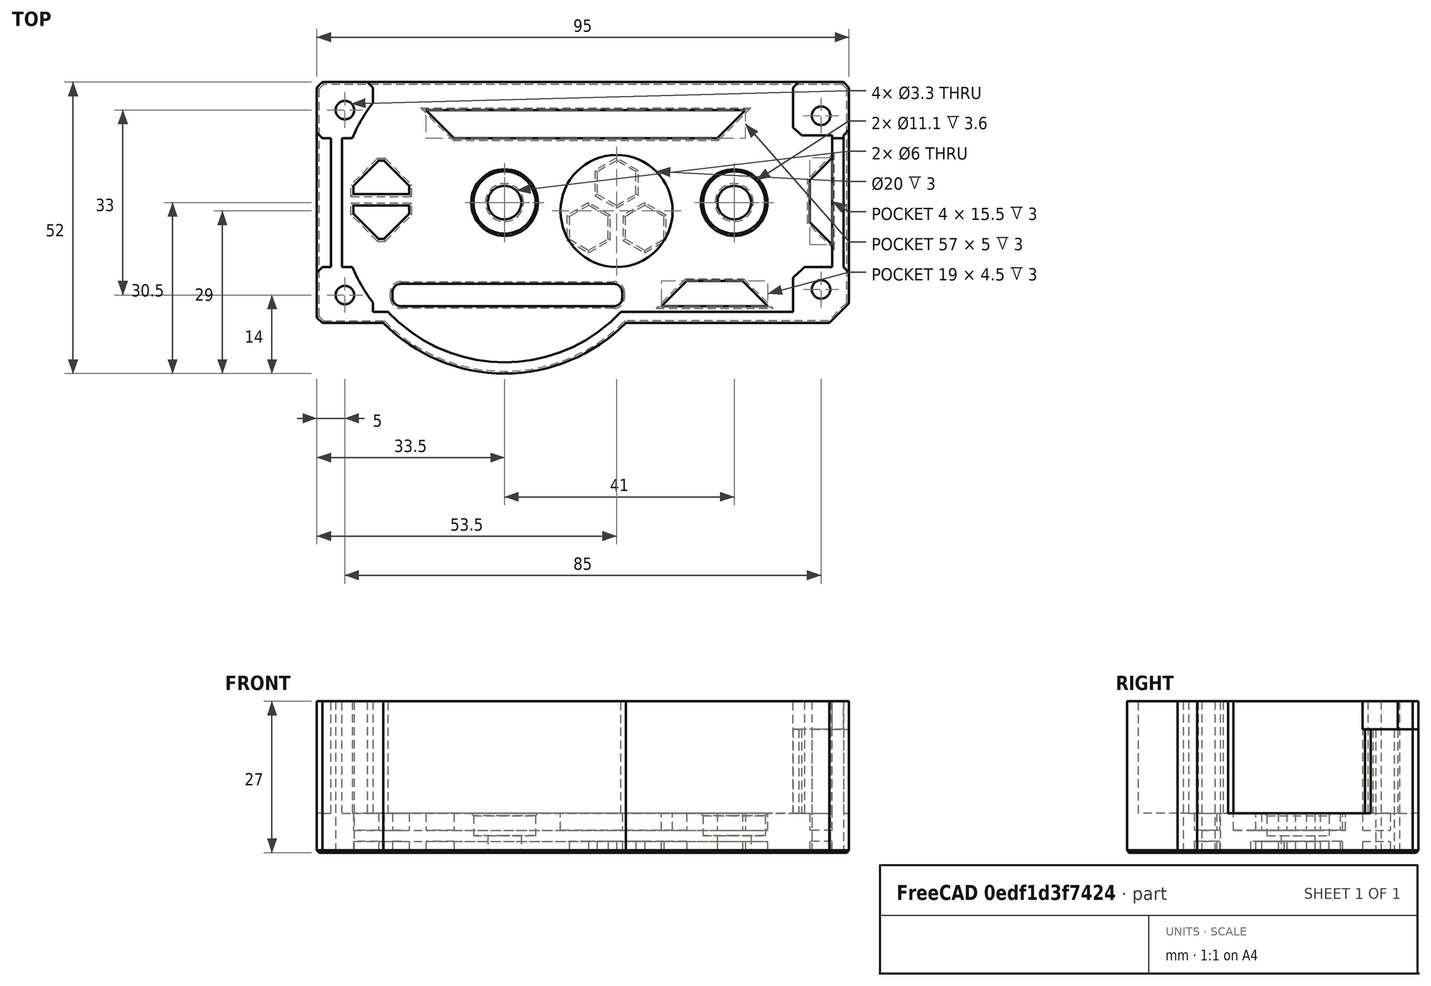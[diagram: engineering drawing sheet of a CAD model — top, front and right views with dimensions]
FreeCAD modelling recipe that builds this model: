
FCSTD DOCUMENT  (FreeCAD 0.19R24291 (Git))
Label: front-plate-type-1
License: Other
LicenseURL: GPL3
objects: Part::Box×14, Part::MultiFuse×6, Part::Chamfer×4, Part::Cylinder×3, Part::Feature×2, Part::Cut×2, Part::Refine×2, Part::MultiCommon×1
note: 34 computed .brp shape members not serialized (recipe doc carries the construction recipe); baked Part::Feature solids carry a one-line shape summary decoded from their .brp

FEATURE [Part::Feature] Chamfer029006001  label="front-plate-type001"
  Placement = pos=(27.5,-8.5,7) rot=(0,1,0;3.14159rad)
  shape: bbox 95 x 43 x 27 mm, 156 faces (baked)
FEATURE [Part::Box] Box  label="Cube"
  AttacherType = Attacher::AttachEngine3D
  Height = 26.5
  Length = 2
  Placement = pos=(-44.5,-12,0.5) rot=(0,0,1;0rad)
  Width = 24
FEATURE [Part::Box] Box001  label="Cube001"
  AttacherType = Attacher::AttachEngine3D
  Height = 7
  Length = 69
  Placement = pos=(-33,16.5,0) rot=(0,0,1;0rad)
  Width = 5
FEATURE [Part::Chamfer] Chamfer
  Base = -> Box001
  Edges = 2 edges r=0.4: [Edge9,Edge11]
FEATURE [Part::Box] Box002  label="Cube002"
  AttacherType = Attacher::AttachEngine3D
  Height = 7
  Length = 28
  Placement = pos=(11,-21.5,0) rot=(0,0,1;0rad)
  Width = 3
FEATURE [Part::Chamfer] Chamfer029006002
  Base = -> Box002
  Edges = 2 edges r=0.4: [Edge9,Edge11]
FEATURE [Part::Box] Box003  label="Cube003"
  AttacherType = Attacher::AttachEngine3D
  Height = 7
  Length = 3
  Placement = pos=(45,-11,0) rot=(0,0,1;0rad)
  Width = 23
FEATURE [Part::Chamfer] Chamfer029006003
  Base = -> Box003
  Edges = 2 edges r=0.4: [Edge4,Edge8]
FEATURE [Part::MultiFuse] Fusion
  Shapes = -> [Chamfer029006001,Chamfer029006002,Chamfer029006003,Chamfer]
FEATURE [Part::Box] Box004  label="Cube004"
  AttacherType = Attacher::AttachEngine3D
  Height = 26.5
  Length = 2
  Placement = pos=(45,-12,0.5) rot=(0,0,1;0rad)
  Width = 23.5
FEATURE [Part::Box] Box005  label="Cube005"
  AttacherType = Attacher::AttachEngine3D
  Height = 21.5
  Length = 2
  Placement = pos=(45,11.5,0.5) rot=(0,0,1;0rad)
  Width = 1.5
FEATURE [Part::Box] Box006  label="Cube006"
  AttacherType = Attacher::AttachEngine3D
  Height = 26.5
  Length = 29
  Placement = pos=(11.5,-21.5,0.5) rot=(0,0,1;0rad)
  Width = 2
FEATURE [Part::Box] Box007  label="Cube007"
  AttacherType = Attacher::AttachEngine3D
  Height = 2
  Length = 12
  Placement = pos=(-41.5,-7,5) rot=(0,0,1;0rad)
  Width = 15
FEATURE [Part::Box] Box008  label="Cube008"
  AttacherType = Attacher::AttachEngine3D
  Height = 2
  Length = 19
  Placement = pos=(-3,-9,5) rot=(0,0,1;0rad)
  Width = 17
FEATURE [Part::Box] Box009  label="Cube009"
  AttacherType = Attacher::AttachEngine3D
  Height = 2
  Length = 69
  Placement = pos=(-34,-19.5,5) rot=(0,0,1;0rad)
  Width = 6
FEATURE [Part::Box] Box010  label="Cube010"
  AttacherType = Attacher::AttachEngine3D
  Height = 2
  Length = 59
  Placement = pos=(-28.5,10.5,5) rot=(0,0,1;0rad)
  Width = 7
FEATURE [Part::Box] Box011  label="Cube011"
  AttacherType = Attacher::AttachEngine3D
  Height = 2
  Length = 6
  Placement = pos=(40.5,-8,5) rot=(0,0,1;0rad)
  Width = 17
FEATURE [Part::MultiFuse] Fusion002
  Placement = pos=(0,0,-3) rot=(0,0,1;0rad)
  Shapes = -> [Box011,Box010,Box009,Box008,Box007]
FEATURE [Part::MultiFuse] Fusion003
  Shapes = -> [Fusion,Fusion002]
FEATURE [Part::Cylinder] Cylinder
  Angle = 360
  AttacherType = Attacher::AttachEngine3D
  Height = 10
  Placement = pos=(6.5,-1.5,4) rot=(0,0,1;0rad)
  Radius = 10
FEATURE [Part::Cut] Cut
  Base = -> Fusion003
  Tool = -> Cylinder
FEATURE [Part::Cylinder] Cylinder002
  Angle = 360
  AttacherType = Attacher::AttachEngine3D
  Height = 30
  Placement = pos=(-13.5,0,7) rot=(0,0,1;0rad)
  Radius = 28.5
FEATURE [Part::Box] Box013  label="Cube013"
  AttacherType = Attacher::AttachEngine3D
  Height = 27
  Length = 50
  Placement = pos=(-38,-21.5,0) rot=(0,0,1;0rad)
  Width = 2
FEATURE [Part::Cylinder] Cylinder004
  Angle = 360
  AttacherType = Attacher::AttachEngine3D
  Height = 27
  Placement = pos=(-13.5,0,0) rot=(0,0,1;0rad)
  Radius = 30.5
FEATURE [Part::Box] Box014  label="Cube014"
  AttacherType = Attacher::AttachEngine3D
  Height = 36
  Length = 50
  Placement = pos=(-38,-32.5,0) rot=(0,0,1;0rad)
  Width = 13
FEATURE [Part::MultiFuse] Fusion005
  Shapes = -> [Box006,Box005,Box004,Box]
FEATURE [Part::MultiFuse] Fusion006
  Shapes = -> [Box013,Cylinder004]
FEATURE [Part::Cut] Cut001
  Base = -> Fusion006
  Tool = -> Cylinder002
FEATURE [Part::MultiCommon] Common
  Shapes = -> [Cut001,Box014]
FEATURE [Part::Refine] Common001
  Source = -> Common
FEATURE [Part::Chamfer] Chamfer029006004
  Base = -> Common001
  Edges = 3 edges r=0.4: [Edge5,Edge10,Edge11]
FEATURE [Part::MultiFuse] Fusion007
  Shapes = -> [Fusion005,Cut,Chamfer029006004]
FEATURE [Part::Refine] Fusion007001
  Source = -> Fusion007
FEATURE [Part::Feature] Fusion007001001  label="face-plate-type1-r2"
  shape: bbox 95 x 52 x 27 mm, 216 faces (baked)
